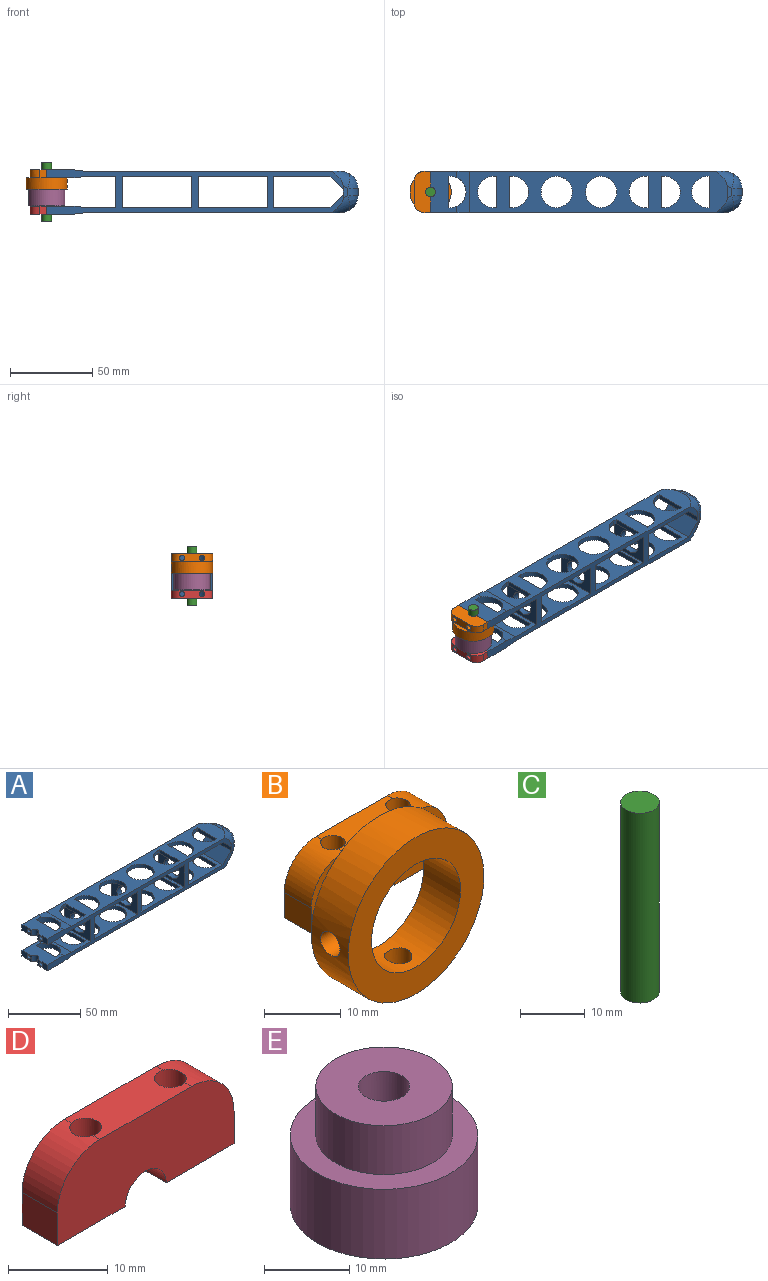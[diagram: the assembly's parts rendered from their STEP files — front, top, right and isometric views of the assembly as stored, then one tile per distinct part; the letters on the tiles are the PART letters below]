
ASSEMBLY  parts=5 mates=5
PART A: 111 faces, bbox 189x31.1x31.1 mm
  f0: plane 42x25mm, normal (0,0,1), area 586.7mm2, adj f6,f8,f31,f32,f33,f34,f35,f43
  f1: plane 34x25mm, normal (0,0,1), area 509.5mm2, adj f6,f8,f18,f19,f20,f21,f26,f27
  f2: plane 42x25mm, normal (0,0,1), area 586.7mm2, adj f6,f8,f22,f23,f24,f25,f30,f44
  f3: plane 9.6x5mm, normal (-1,0,0), area 40mm2, adj f6,f9,f11,f17,f40
  f4: plane 25x18.4mm, normal (0,0,1), area 280.3mm2, adj f6,f8,f12,f36,f37,f38,f39,f42
  f5: plane 156.4x25mm, normal (0,0,-1), area 2422.1mm2, adj f6,f8,f10,f18,f19,f20,f21,f22
  f6: plane 180x27mm, normal (0,1,0), area 1410.1mm2, adj f0,f1,f2,f3,f4,f5,f9,f10
  f7: plane 9.6x5mm, normal (-1,0,0), area 40mm2, adj f8,f9,f11,f17,f41
  f8: plane 180x27mm, normal (0,-1,0), area 1410.1mm2, adj f0,f1,f2,f4,f5,f7,f9,f10
  f9: plane 25x16mm, normal (0,0,-1), area 294.1mm2, adj f3,f6,f7,f8,f10,f13,f14,f15
  f10: plane 25x7.6mm, normal (0.13,0,-0.99), area 122.9mm2, adj f5,f6,f8,f9,f15
  f11: plane 25x16mm, normal (0,0,1), area 294.1mm2, adj f3,f6,f7,f8,f12,f13,f14,f15
  f12: plane 25x7.6mm, normal (0.13,0,0.99), area 122.9mm2, adj f4,f6,f8,f11,f15
  f13: plane 19x5mm, normal (1,0,0), area 78.9mm2, adj f9,f11,f14,f16,f40,f41
  f14: plane 5x1mm, normal (0,1,0), area 5mm2, adj f9,f11,f13,f15
  f15: cylinder r=9.5mm len=19mm, axis (0,0,1), area 128.9mm2, adj f9,f10,f11,f12,f14,f16
  f16: plane 5x1mm, normal (0,-1,0), area 5mm2, adj f9,f11,f13,f15
  f17: cylinder r=2.9mm len=5.8mm, axis (0,0,1), area 45.6mm2, adj f3,f7,f9,f11
  f18: plane 19x3mm, normal (1,0,0), area 57mm2, adj f1,f5,f19,f21
  f19: plane 3x2mm, normal (0,1,0), area 6mm2, adj f1,f5,f18,f20
  f20: cylinder r=9.5mm len=19mm, axis (0,0,1), area 89.5mm2, adj f1,f5,f19,f21
  f21: plane 3x2mm, normal (0,-1,0), area 6mm2, adj f1,f5,f18,f20
  f22: plane 3x2mm, normal (0,1,0), area 6mm2, adj f2,f5,f23,f25
  f23: plane 19x3mm, normal (-1,0,0), area 57mm2, adj f2,f5,f22,f24
  f24: plane 3x2mm, normal (0,-1,0), area 6mm2, adj f2,f5,f23,f25
  f25: cylinder r=9.5mm len=19mm, axis (0,0,1), area 89.5mm2, adj f2,f5,f22,f24
  f26: plane 3x1mm, normal (0,1,0), area 3mm2, adj f1,f5,f27,f29
  f27: plane 19x3mm, normal (-1,0,0), area 57mm2, adj f1,f5,f26,f28
  f28: plane 3x1mm, normal (0,-1,0), area 3mm2, adj f1,f5,f27,f29
  f29: cylinder r=9.5mm len=19mm, axis (0,0,1), area 89.5mm2, adj f1,f5,f26,f28
  f30: cylinder r=9.5mm len=19mm, axis (0,0,1), area 179.1mm2, adj f2,f5
  f31: cylinder r=9.5mm len=19mm, axis (0,0,1), area 179.1mm2, adj f0,f5
  f32: cylinder r=9.5mm len=19mm, axis (0,0,1), area 89.5mm2, adj f0,f5,f33,f35
  f33: plane 3x2mm, normal (0,-1,0), area 6mm2, adj f0,f5,f32,f34
  f34: plane 19x3mm, normal (1,0,0), area 57mm2, adj f0,f5,f33,f35
  f35: plane 3x2mm, normal (0,1,0), area 6mm2, adj f0,f5,f32,f34
  f36: plane 3x2mm, normal (0,1,0), area 6mm2, adj f4,f5,f37,f39
  f37: plane 19x3mm, normal (-1,0,0), area 57mm2, adj f4,f5,f36,f38
  f38: plane 3x2mm, normal (0,-1,0), area 6mm2, adj f4,f5,f37,f39
  f39: cylinder r=9.5mm len=19mm, axis (0,0,1), area 89.5mm2, adj f4,f5,f36,f38
  f40: cylinder r=1.6mm len=11mm, axis (-1,0,0), area 110.6mm2, adj f3,f13
  f41: cylinder r=1.6mm len=11mm, axis (-1,0,0), area 110.6mm2, adj f7,f13
  f42: plane 25x19mm, normal (-1,0,0), area 298.3mm2, adj f4,f6,f8,f52,f90
  f43: plane 25x19mm, normal (1,0,0), area 298.3mm2, adj f0,f6,f8,f48,f90
  f44: plane 25x19mm, normal (-1,0,0), area 298.3mm2, adj f2,f6,f8,f50,f89
  f45: plane 25x19mm, normal (1,0,0), area 298.3mm2, adj f1,f6,f8,f49,f89
  f46: plane 25x19mm, normal (-1,0,0), area 298.3mm2, adj f0,f6,f8,f48,f88
  f47: plane 25x19mm, normal (1,0,0), area 298.3mm2, adj f2,f6,f8,f50,f88
  f48: plane 42x25mm, normal (0,0,-1), area 586.7mm2, adj f6,f8,f43,f46,f77,f78,f79,f80
  f49: plane 34x25mm, normal (0,0,-1), area 509.5mm2, adj f6,f8,f45,f64,f65,f66,f67,f72
  f50: plane 42x25mm, normal (0,0,-1), area 586.7mm2, adj f6,f8,f44,f47,f68,f69,f70,f71
  f51: plane 9.6x5mm, normal (-1,0,0), area 40mm2, adj f6,f55,f57,f63,f86
  f52: plane 25x18.4mm, normal (0,0,-1), area 280.3mm2, adj f6,f8,f42,f58,f82,f83,f84,f85
  f53: plane 156.4x25mm, normal (0,0,1), area 2422.1mm2, adj f6,f8,f56,f64,f65,f66,f67,f68
  f54: plane 9.6x5mm, normal (-1,0,0), area 40mm2, adj f8,f55,f57,f63,f87
  f55: plane 25x16mm, normal (0,0,1), area 294.1mm2, adj f6,f8,f51,f54,f56,f59,f60,f61
  f56: plane 25x7.6mm, normal (0.13,0,0.99), area 122.9mm2, adj f6,f8,f53,f55,f61
  f57: plane 25x16mm, normal (0,0,-1), area 294.1mm2, adj f6,f8,f51,f54,f58,f59,f60,f61
  f58: plane 25x7.6mm, normal (0.13,0,-0.99), area 122.9mm2, adj f6,f8,f52,f57,f61
  f59: plane 19x5mm, normal (1,0,0), area 78.9mm2, adj f55,f57,f60,f62,f86,f87
  f60: plane 5x1mm, normal (0,1,0), area 5mm2, adj f55,f57,f59,f61
  f61: cylinder r=9.5mm len=19mm, axis (0,0,-1), area 128.9mm2, adj f55,f56,f57,f58,f60,f62
  f62: plane 5x1mm, normal (0,-1,0), area 5mm2, adj f55,f57,f59,f61
  f63: cylinder r=2.9mm len=5.8mm, axis (0,0,-1), area 45.6mm2, adj f51,f54,f55,f57
  f64: plane 19x3mm, normal (1,0,0), area 57mm2, adj f49,f53,f65,f67
  f65: plane 3x2mm, normal (0,1,0), area 6mm2, adj f49,f53,f64,f66
  f66: cylinder r=9.5mm len=19mm, axis (0,0,-1), area 89.5mm2, adj f49,f53,f65,f67
  f67: plane 3x2mm, normal (0,-1,0), area 6mm2, adj f49,f53,f64,f66
  f68: plane 3x2mm, normal (0,1,0), area 6mm2, adj f50,f53,f69,f71
  f69: plane 19x3mm, normal (-1,0,0), area 57mm2, adj f50,f53,f68,f70
  f70: plane 3x2mm, normal (0,-1,0), area 6mm2, adj f50,f53,f69,f71
  f71: cylinder r=9.5mm len=19mm, axis (0,0,-1), area 89.5mm2, adj f50,f53,f68,f70
  f72: plane 3x1mm, normal (0,1,0), area 3mm2, adj f49,f53,f73,f75
  f73: plane 19x3mm, normal (-1,0,0), area 57mm2, adj f49,f53,f72,f74
  f74: plane 3x1mm, normal (0,-1,0), area 3mm2, adj f49,f53,f73,f75
  f75: cylinder r=9.5mm len=19mm, axis (0,0,-1), area 89.5mm2, adj f49,f53,f72,f74
  f76: cylinder r=9.5mm len=19mm, axis (0,0,-1), area 179.1mm2, adj f50,f53
  f77: cylinder r=9.5mm len=19mm, axis (0,0,-1), area 179.1mm2, adj f48,f53
  f78: cylinder r=9.5mm len=19mm, axis (0,0,-1), area 89.5mm2, adj f48,f53,f79,f81
  f79: plane 3x2mm, normal (0,-1,0), area 6mm2, adj f48,f53,f78,f80
  f80: plane 19x3mm, normal (1,0,0), area 57mm2, adj f48,f53,f79,f81
  f81: plane 3x2mm, normal (0,1,0), area 6mm2, adj f48,f53,f78,f80
  f82: plane 3x2mm, normal (0,1,0), area 6mm2, adj f52,f53,f83,f85
  f83: plane 19x3mm, normal (-1,0,0), area 57mm2, adj f52,f53,f82,f84
  f84: plane 3x2mm, normal (0,-1,0), area 6mm2, adj f52,f53,f83,f85
  f85: cylinder r=9.5mm len=19mm, axis (0,0,-1), area 89.5mm2, adj f52,f53,f82,f84
  f86: cylinder r=1.6mm len=11mm, axis (-1,0,0), area 110.6mm2, adj f51,f59
  f87: cylinder r=1.6mm len=11mm, axis (-1,0,0), area 110.6mm2, adj f54,f59
  f88: cylinder r=7.5mm len=15mm, axis (1,0,0), area 188.5mm2, adj f46,f47
  f89: cylinder r=7.5mm len=15mm, axis (1,0,0), area 188.5mm2, adj f44,f45
  f90: cylinder r=7.5mm len=15mm, axis (1,0,0), area 188.5mm2, adj f42,f43
  f91: plane 25x3mm, normal (-1,0,0), area 75mm2, adj f92,f94,f109,f110
  f92: plane 7.01x2.75mm, normal (0.37,0.93,0), area 17.5mm2, adj f6,f91,f97,f101,f108
  f93: plane 7.01x2.75mm, normal (0.37,0,0.93), area 17.5mm2, adj f53,f99,f101,f103
  f94: plane 7.01x2.75mm, normal (0.37,-0.93,0), area 17.5mm2, adj f8,f91,f100,f103,f105
  f95: plane 7.01x2.75mm, normal (0.37,0,-0.93), area 17.5mm2, adj f5,f98,f105,f108
  f96: plane 4.24x4.24mm, normal (1,0,0), area 18mm2, adj f97,f98,f99,f100
  f97: cylinder r=10mm len=9.27mm, axis (0,0,1), area 53.6mm2, adj f92,f96,f102,f107
  f98: cylinder r=10mm len=9.27mm, axis (0,1,0), area 53.6mm2, adj f95,f96,f106,f107
  f99: cylinder r=10mm len=9.27mm, axis (0,-1,0), area 53.6mm2, adj f93,f96,f102,f104
  f100: cylinder r=10mm len=9.27mm, axis (0,0,1), area 53.6mm2, adj f94,f96,f104,f106
  f101: cylinder r=9.7mm len=13.14mm, axis (-0.87,0.35,0.35), area 90.7mm2, adj f6,f53,f92,f93,f102
  f102: bspline ~9.66x9.66mm, area 81.4mm2, adj f97,f99,f101
  f103: cylinder r=9.7mm len=13.14mm, axis (-0.87,-0.35,0.35), area 90.7mm2, adj f8,f53,f93,f94,f104
  f104: bspline ~9.66x9.66mm, area 83.6mm2, adj f99,f100,f103
  f105: cylinder r=9.7mm len=13.14mm, axis (-0.87,-0.35,-0.35), area 90.7mm2, adj f5,f8,f94,f95,f106
  f106: bspline ~9.66x9.66mm, area 83.6mm2, adj f98,f100,f105
  f107: bspline ~9.66x9.66mm, area 81.4mm2, adj f97,f98,f108
  f108: cylinder r=9.7mm len=13.14mm, axis (-0.87,0.35,-0.35), area 90.7mm2, adj f5,f6,f92,f95,f107
  f109: plane 25x8mm, normal (-0.71,0,0.71), area 282.8mm2, adj f1,f6,f8,f91
  f110: plane 25x8mm, normal (-0.71,0,-0.71), area 282.8mm2, adj f6,f8,f49,f91
PART B: 21 faces, bbox 25x11.8x25 mm
  f0: plane 16.4x8.2mm, normal (0,-1,0), area 92.4mm2, adj f2,f8,f13,f16
  f1: plane 9.89x4.86mm, normal (0,-1,0), area 7.4mm2, adj f6,f12,f17
  f2: plane 9.6x5mm, normal (0,0,-1), area 40mm2, adj f0,f3,f4,f10,f13,f14
  f3: plane 25x10mm, normal (0,1,0), area 221.3mm2, adj f2,f4,f6,f7,f8,f11,f12,f13
  f4: plane 5x4mm, normal (-1,0,0), area 20mm2, adj f2,f3,f5,f11
  f5: plane 9.89x4.86mm, normal (0,-1,0), area 7.4mm2, adj f4,f11,f17
  f6: plane 5x4mm, normal (1,0,0), area 20mm2, adj f1,f3,f8,f12
  f7: plane 13x5mm, normal (0,0,1), area 53.8mm2, adj f3,f9,f10,f11,f12,f15
  f8: plane 9.6x5mm, normal (0,0,-1), area 40mm2, adj f0,f3,f6,f9,f13,f14
  f9: cylinder r=1.6mm len=10mm, axis (0,0,1), area 100.3mm2, adj f7,f8,f12
  f10: cylinder r=1.6mm len=10mm, axis (0,0,1), area 100.3mm2, adj f2,f7,f11
  f11: cylinder r=6mm len=6mm, axis (0,1,0), area 44.7mm2, adj f3,f4,f5,f7,f10,f15
  f12: cylinder r=6mm len=6mm, axis (0,-1,0), area 44.7mm2, adj f1,f3,f6,f7,f9,f15
  f13: cylinder r=2.9mm len=5.8mm, axis (0,-1,0), area 45.6mm2, adj f0,f2,f3,f8
  f14: plane 25x12.5mm, normal (0,1,0), area 139.8mm2, adj f2,f8,f16,f17
  f15: plane 15.29x2.61mm, normal (0,1,0), area 25.6mm2, adj f7,f11,f12,f17
  f16: cylinder r=8.2mm len=16.4mm, axis (0,1,0), area 329.9mm2, adj f0,f14,f18,f19,f20
  f17: cylinder r=12.5mm len=25mm, axis (0,1,0), area 513.6mm2, adj f1,f5,f14,f15,f18,f19,f20
  f18: plane 25x25mm, normal (0,-1,0), area 279.6mm2, adj f16,f17
  f19: cylinder r=1.8mm len=4.5mm, axis (1,0,0), area 49mm2, adj f16,f17
  f20: cylinder r=1.8mm len=4.5mm, axis (0,0,1), area 49mm2, adj f16,f17
PART C: 3 faces, bbox 6x6x36 mm
  f0: cylinder r=3mm len=36mm, axis (0,0,-1), area 678.6mm2, adj f1,f2
  f1: plane 6x6mm, normal (0,0,1), area 28.3mm2, adj f0
  f2: plane 6x6mm, normal (0,0,-1), area 28.3mm2, adj f0
PART D: 12 faces, bbox 25x5x10 mm
  f0: plane 9.6x5mm, normal (0,0,-1), area 40mm2, adj f1,f2,f3,f8,f11
  f1: plane 25x10mm, normal (0,1,0), area 221.3mm2, adj f0,f2,f4,f5,f6,f9,f10,f11
  f2: plane 5x4mm, normal (-1,0,0), area 20mm2, adj f0,f1,f3,f9
  f3: plane 25x10mm, normal (0,-1,0), area 221.3mm2, adj f0,f2,f4,f5,f6,f9,f10,f11
  f4: plane 5x4mm, normal (1,0,0), area 20mm2, adj f1,f3,f6,f10
  f5: plane 13x5mm, normal (0,0,1), area 53.8mm2, adj f1,f3,f7,f8,f9,f10
  f6: plane 9.6x5mm, normal (0,0,-1), area 40mm2, adj f1,f3,f4,f7,f11
  f7: cylinder r=1.6mm len=10mm, axis (0,0,1), area 100.3mm2, adj f5,f6,f10
  f8: cylinder r=1.6mm len=10mm, axis (0,0,1), area 100.3mm2, adj f0,f5,f9
  f9: cylinder r=6mm len=6mm, axis (0,1,0), area 44.7mm2, adj f1,f2,f3,f5,f8
  f10: cylinder r=6mm len=6mm, axis (0,-1,0), area 44.7mm2, adj f1,f3,f4,f5,f7
  f11: cylinder r=2.9mm len=5.8mm, axis (0,-1,0), area 45.6mm2, adj f0,f1,f3,f6
PART E: 6 faces, bbox 22x22x17 mm
  f0: cylinder r=8mm len=16mm, axis (0,0,-1), area 351.9mm2, adj f1,f4
  f1: plane 16x16mm, normal (0,0,1), area 172.8mm2, adj f0,f5
  f2: cylinder r=11mm len=22mm, axis (0,0,1), area 691.2mm2, adj f3,f4
  f3: plane 22x22mm, normal (0,0,-1), area 351.9mm2, adj f2,f5
  f4: plane 22x22mm, normal (0,0,1), area 179.1mm2, adj f0,f2
  f5: cylinder r=3mm len=17mm, axis (0,0,-1), area 320.4mm2, adj f1,f3
PLACE A rot(axis=(1,0,0),0deg) t=(-45.28,-0.06,-29.32)mm
PLACE B rot(axis=(0.58,-0.58,-0.58),120deg) t=(-135.28,-0.07,-7.32)mm
PLACE C rot(axis=(1,0,0),0deg) t=(-135.28,-0.06,-18.32)mm fixed
PLACE D rot(axis=(-0.58,-0.58,0.58),120deg) t=(-135.28,-0.06,-29.32)mm
PLACE E rot(axis=(1,0,0),0deg) t=(-135.28,-0.06,-16.72)mm
MATE fastened A.f41 <-> D.f8  axis (-1,0,0) through (-135.28,-6.06,-29.32)mm
MATE fastened C.f0 <-> E.f2  axis (0,0,-1) through (-135.28,-0.06,-18.32)mm
MATE fastened A.f40 <-> D.f7  axis (-1,0,0) through (-135.28,5.94,-29.32)mm
MATE slider A.f17 <-> C.f0  axis (0,0,1) through (-135.28,-0.07,-4.82)mm
MATE fastened B.f10 <-> A.f86  axis (-1,0,0) through (-135.28,5.93,-7.32)mm
